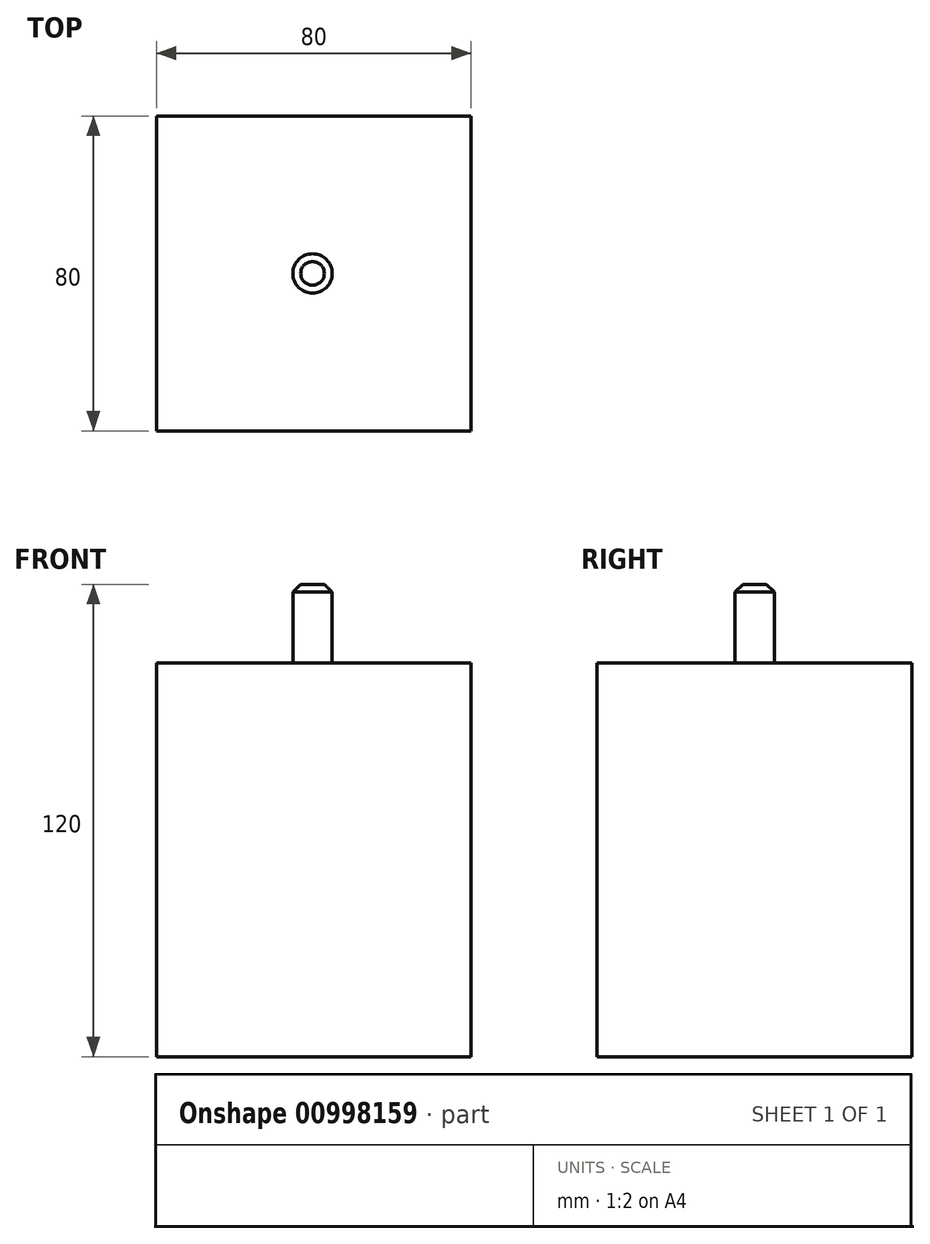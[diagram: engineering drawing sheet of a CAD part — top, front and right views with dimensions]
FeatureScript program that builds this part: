
annotation { "Feature Type Name" : "Feature", "Feature Type Description" : "" }
export const myFeature = defineFeature(function(context is Context, id is Id, definition is map)
    precondition{}
    {
        {
            var Q0;
            Q0=qCreatedBy(makeId("Top.planeOp"),FACE);
            var sketch = newSketch(context, id + "F0", { "sketchPlane" : qUnion([Q0])});
            skLineSegment(sketch, "E0.bottom", {"start": v(-39.69, 42.07) * mm, "end": v(40.31, 42.07) * mm});
            skLineSegment(sketch, "E0.top", {"start": v(-39.69, -37.93) * mm, "end": v(40.31, -37.93) * mm});
            skLineSegment(sketch, "E0.left", {"start": v(-39.69, 42.07) * mm, "end": v(-39.69, -37.93) * mm});
            skLineSegment(sketch, "E0.right", {"start": v(40.31, 42.07) * mm, "end": v(40.31, -37.93) * mm});
            skSolve(sketch);
        }
        {
            var Q0;
            Q0=makeQuery(id+"F0.imprint","IMPRINT",FACE,{"disambiguationData":[TD([[makeQuery(id+"F0.imprint","IMPRINT",EDGE,{"derivedFrom":sQuery(id+"F0.wireOp",EDGE,"E0.bottom")}),-1.0]])]});
            extrude(context, id + "F1", {"entities" : qUnion([Q0]), "depth" : 100 * mm, "offsetDistance" : 25 * mm});
        }
        {
            var Q0;
            Q0=makeQuery(id+"F1.opExtrude","CAP_FACE",FACE,{"disambiguationData":[OSD([sQuery(id+"F0.wireOp",EDGE,"E0.bottom"),sQuery(id+"F0.wireOp",EDGE,"E0.top"),sQuery(id+"F0.wireOp",EDGE,"E0.left"),sQuery(id+"F0.wireOp",EDGE,"E0.right")])],"isStart":false});
            var sketch = newSketch(context, id + "F2", { "sketchPlane" : qUnion([Q0])});
            skCircle(sketch, "E1", {"center": v(0, 2.07) * mm, "radius": 5 * mm});
            skSolve(sketch);
        }
        {
            var Q0;
            Q0=makeQuery(id+"F2.imprint","IMPRINT",FACE,{"disambiguationData":[TD([[makeQuery(id+"F2.imprint","IMPRINT",EDGE,{"derivedFrom":sQuery(id+"F2.wireOp",EDGE,"E1")}),1.0]])]});
            extrude(context, id + "F3", {"entities" : qUnion([Q0]), "operationType" : NewBodyOperationType.ADD, "depth" : 20 * mm, "offsetDistance" : 25 * mm});
        }
        {
            var Q0;
            Q0=makeQuery(id+"F3.opExtrude","CAP_EDGE",EDGE,{"disambiguationData":[OSD([sQuery(id+"F2.wireOp",EDGE,"E1")])],"isStart":false});
            chamfer(context, id + "F4", {"entities" : qUnion([Q0]), "width" : 2 * mm, "tangentPropagation" : true});
        }
    });
